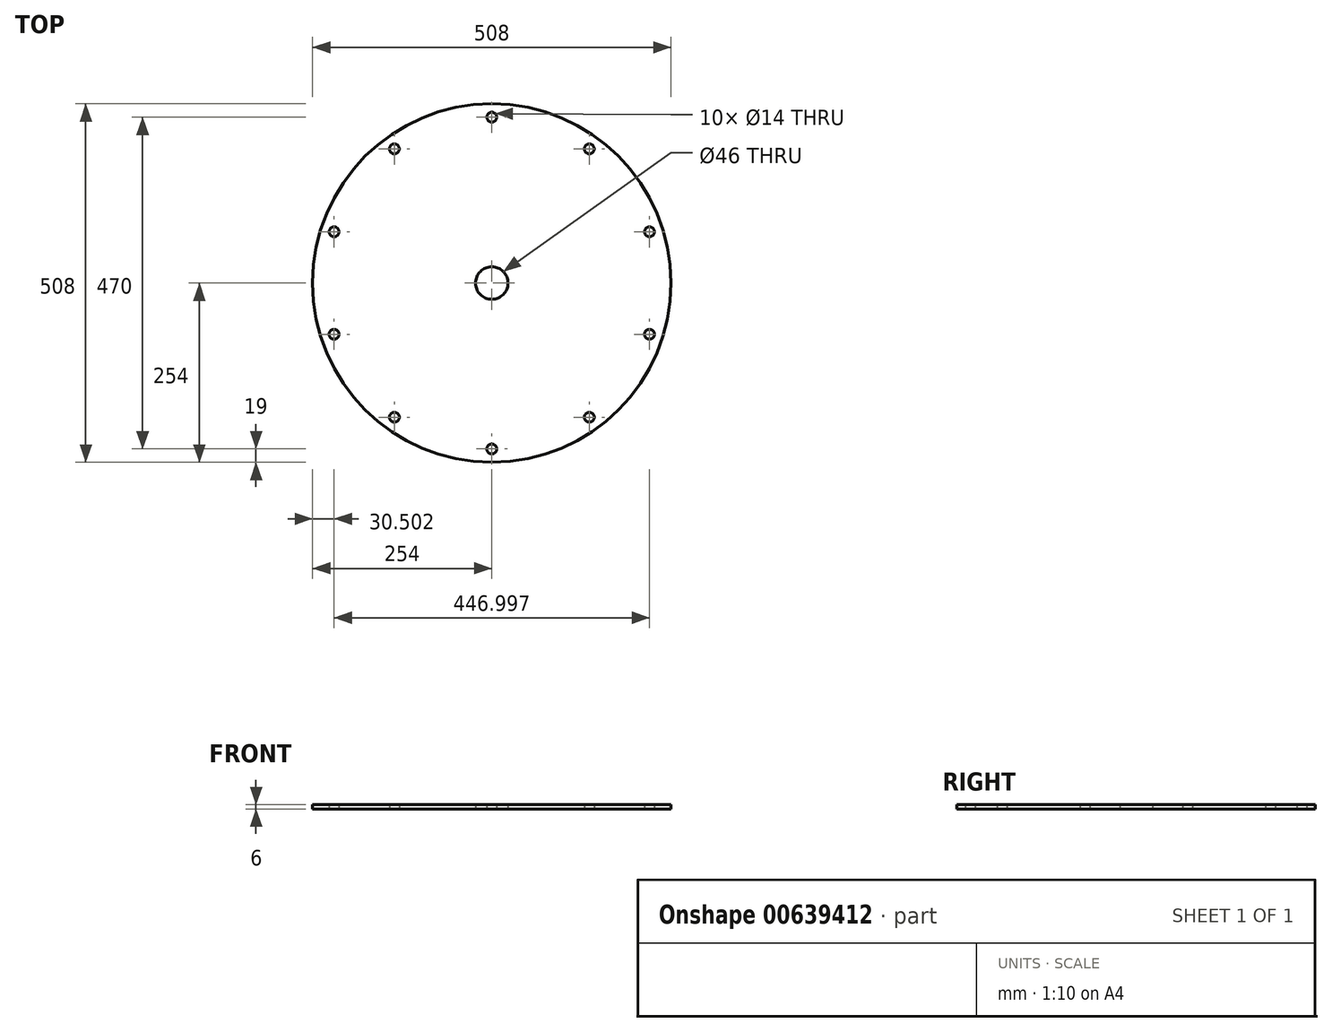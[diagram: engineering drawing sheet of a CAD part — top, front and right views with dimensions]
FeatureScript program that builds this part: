
annotation { "Feature Type Name" : "Feature", "Feature Type Description" : "" }
export const myFeature = defineFeature(function(context is Context, id is Id, definition is map)
    precondition{}
    {
        {
            var Q0;
            Q0=qCreatedBy(makeId("Top.planeOp"),FACE);
            var sketch = newSketch(context, id + "F0", { "sketchPlane" : qUnion([Q0])});
            skCircle(sketch, "E0", {"center": v(0, 0) * mm, "radius": 254 * mm});
            skCircle(sketch, "E1", {"center": v(0, 0) * mm, "radius": 23 * mm});
            skCircle(sketch, "E2", {"center": v(0, 0) * mm, "radius": 235 * mm, "construction": true});
            skCircle(sketch, "E3", {"center": v(0, 235) * mm, "radius": 7 * mm});
            skCircle(sketch, "E4.1.0", {"center": v(-138.13, 190.12) * mm, "radius": 7 * mm});
            skCircle(sketch, "E4.2.0", {"center": v(-223.5, 72.62) * mm, "radius": 7 * mm});
            skCircle(sketch, "E4.3.0", {"center": v(-223.5, -72.62) * mm, "radius": 7 * mm});
            skCircle(sketch, "E4.4.0", {"center": v(-138.13, -190.12) * mm, "radius": 7 * mm});
            skCircle(sketch, "E4.5.0", {"center": v(0, -235) * mm, "radius": 7 * mm});
            skCircle(sketch, "E4.6.0", {"center": v(138.13, -190.12) * mm, "radius": 7 * mm});
            skCircle(sketch, "E4.7.0", {"center": v(223.5, -72.62) * mm, "radius": 7 * mm});
            skCircle(sketch, "E4.8.0", {"center": v(223.5, 72.62) * mm, "radius": 7 * mm});
            skCircle(sketch, "E4.9.0", {"center": v(138.13, 190.12) * mm, "radius": 7 * mm});
            skSolve(sketch);
        }
        {
            var Q0;
            Q0=makeQuery(id+"F0.imprint","IMPRINT",FACE,{"disambiguationData":[TD([[makeQuery(id+"F0.imprint","IMPRINT",EDGE,{"derivedFrom":sQuery(id+"F0.wireOp",EDGE,"E0")}),1.0]])]});
            extrude(context, id + "F1", {"entities" : qUnion([Q0]), "depth" : 6 * mm, "offsetDistance" : 25 * mm});
        }
    });
